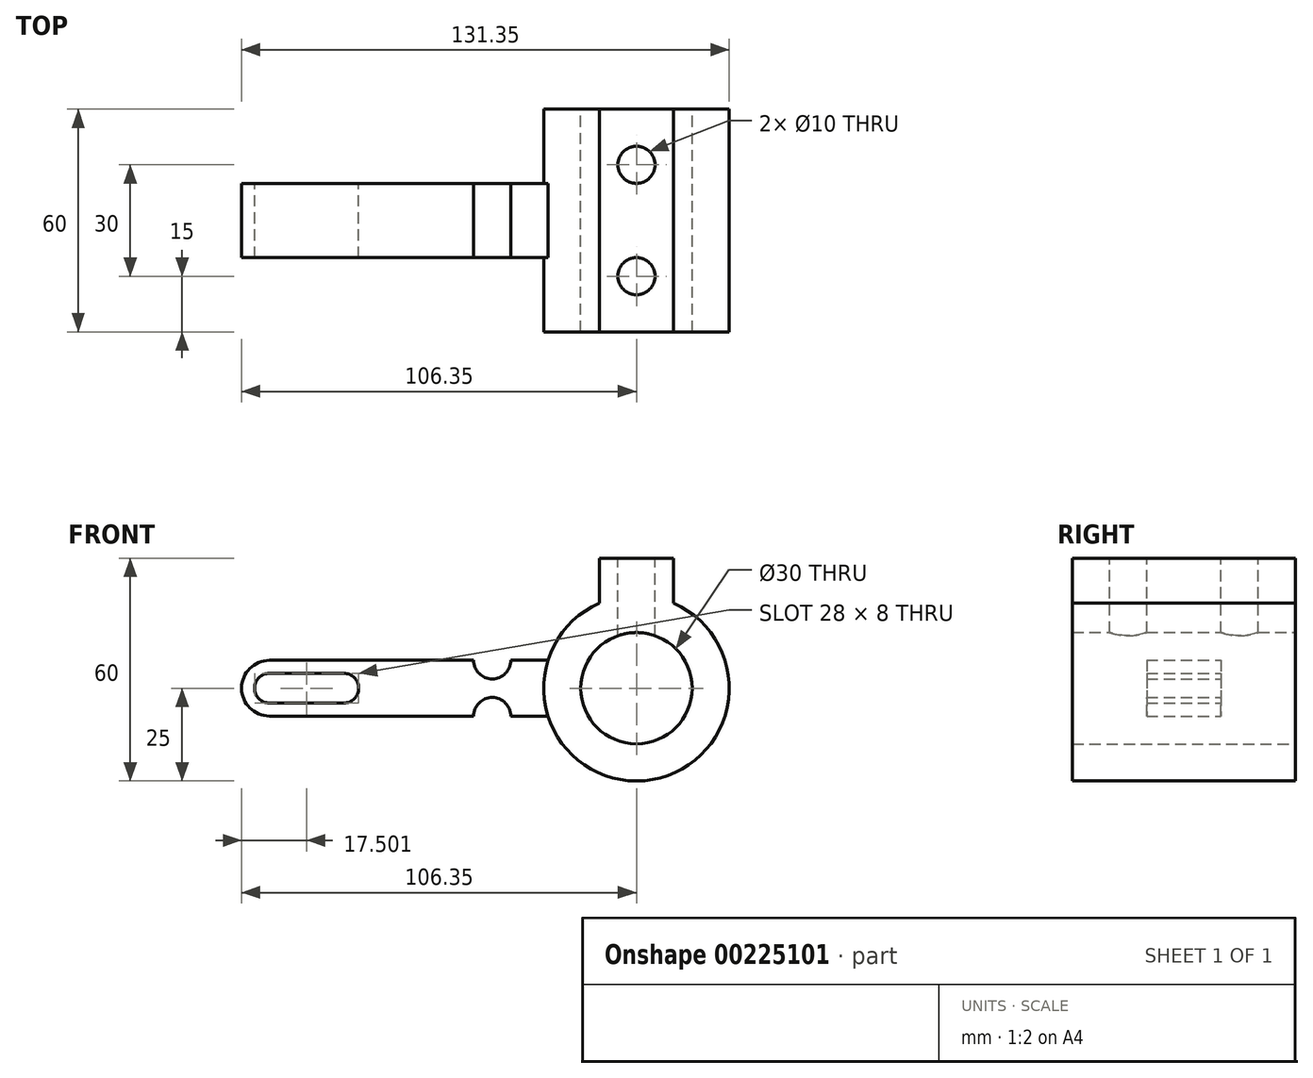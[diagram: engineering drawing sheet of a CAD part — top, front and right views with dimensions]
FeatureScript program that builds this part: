
annotation { "Feature Type Name" : "Feature", "Feature Type Description" : "" }
export const myFeature = defineFeature(function(context is Context, id is Id, definition is map)
    precondition{}
    {
        {
            var Q0;
            Q0=qCreatedBy(makeId("Front.planeOp"),FACE);
            var sketch = newSketch(context, id + "F0", { "sketchPlane" : qUnion([Q0])});
            skCircle(sketch, "E0", {"center": v(0, 0) * mm, "radius": 25 * mm});
            skCircle(sketch, "E1", {"center": v(0, 0) * mm, "radius": 15 * mm});
            skLineSegment(sketch, "E2.bottom", {"start": v(10, 15) * mm, "end": v(-10, 15) * mm});
            skLineSegment(sketch, "E2.top", {"start": v(10, 35) * mm, "end": v(-10, 35) * mm});
            skLineSegment(sketch, "E2.left", {"start": v(10, 15) * mm, "end": v(10, 35) * mm});
            skLineSegment(sketch, "E2.right", {"start": v(-10, 15) * mm, "end": v(-10, 35) * mm});
            skPoint(sketch, "E2.middle", {"position": v(0, 25) * mm});
            skLineSegment(sketch, "E3", {"start": v(-124.07, 0) * mm, "end": v(52.52, 0) * mm, "construction": true});
            skLineSegment(sketch, "E4", {"start": v(-124.07, 0) * mm, "end": v(-185.63, 0) * mm, "construction": true});
            skLineSegment(sketch, "E5.bottom", {"start": v(-23.85, 7.5) * mm, "end": v(-33.85, 7.5) * mm});
            skLineSegment(sketch, "E5.top", {"start": v(-23.85, -7.5) * mm, "end": v(-33.85, -7.5) * mm});
            skLineSegment(sketch, "E5.left", {"start": v(-23.85, 7.5) * mm, "end": v(-23.85, -7.5) * mm});
            skLineSegment(sketch, "E5.right", {"start": v(-98.85, 7.5) * mm, "end": v(-98.85, -7.5) * mm, "construction": true});
            skLineSegment(sketch, "E6", {"start": v(-38.85, 15.12) * mm, "end": v(-38.85, -23.72) * mm, "construction": true});
            skArc(sketch, "E7", {"start": v(-43.85, 7.5) * mm, "mid": v(-38.85, 2.5) * mm, "end": v(-33.85, 7.5) * mm});
            skArc(sketch, "E8", {"start": v(-33.85, -7.5) * mm, "mid": v(-38.85, -2.5) * mm, "end": v(-43.85, -7.5) * mm});
            skLineSegment(sketch, "E9.trimOffspring", {"start": v(-43.85, 7.5) * mm, "end": v(-98.85, 7.5) * mm});
            skLineSegment(sketch, "E10.trimOffspring", {"start": v(-43.85, -7.5) * mm, "end": v(-98.85, -7.5) * mm});
            skLineSegment(sketch, "E11", {"start": v(-78.85, 16.94) * mm, "end": v(-78.85, -16.42) * mm, "construction": true});
            skArc(sketch, "E12", {"start": v(-98.85, 7.5) * mm, "mid": v(-106.35, 0) * mm, "end": v(-98.85, -7.5) * mm});
            skArc(sketch, "E13", {"start": v(-98.85, 4) * mm, "mid": v(-102.85, 0) * mm, "end": v(-98.85, -4) * mm});
            skLineSegment(sketch, "E14", {"start": v(-98.85, 4) * mm, "end": v(-78.85, 4) * mm});
            skLineSegment(sketch, "E15", {"start": v(-98.85, -4) * mm, "end": v(-78.85, -4) * mm});
            skArc(sketch, "E16", {"start": v(-78.85, -4) * mm, "mid": v(-74.85, 0) * mm, "end": v(-78.85, 4) * mm});
            skPoint(sketch, "E16.centerSnap0", {"position": v(-78.85, 0.26) * mm});
            skSolve(sketch);
        }
        {
            var Q0;
            {var subQ3=sQuery(id+"F0.wireOp",EDGE,"E1");Q0=makeQuery(id+"F0.imprint","IMPRINT",FACE,{"disambiguationData":[TD([[makeQuery(id+"F0.imprint","IMPRINT",EDGE,{"derivedFrom":subQ3}),-1.0]])]});}
            var Q1;
            {var subQ3=sQuery(id+"F0.wireOp",EDGE,"E0");var subQ5=sQuery(id+"F0.wireOp",EDGE,"E2.right");var subQ8=makeQuery(id+"F0.imprint","INTERSECT",VERTEX,{"derivedFrom":[subQ3,subQ5]});Q1=makeQuery(id+"F0.imprint","IMPRINT",FACE,{"disambiguationData":[TD([[makeQuery(id+"F0.imprint","IMPRINT",EDGE,{"disambiguationData":[TD([[subQ8,1.0]])],"derivedFrom":subQ3}),1.0]])]});}
            var Q2;
            {var subQ0=sQuery(id+"F0.wireOp",EDGE,"E5.left");Q2=makeQuery(id+"F0.imprint","IMPRINT",FACE,{"disambiguationData":[TD([[makeQuery(id+"F0.imprint","IMPRINT",EDGE,{"derivedFrom":subQ0}),-1.0]])]});}
            var Q3;
            {var subQ5=sQuery(id+"F0.wireOp",EDGE,"E2.top");Q3=makeQuery(id+"F0.imprint","IMPRINT",FACE,{"disambiguationData":[TD([[makeQuery(id+"F0.imprint","IMPRINT",EDGE,{"derivedFrom":subQ5}),1.0]])]});}
            extrude(context, id + "F1", {"entities" : qUnion([Q0, Q1, Q2, Q3]), "endBound" : BoundingType.SYMMETRIC, "depth" : 60 * mm});
        }
        {
            var Q0;
            {var subQ1=sQuery(id+"F0.wireOp",EDGE,"E5.bottom");Q0=makeQuery(id+"F0.imprint","IMPRINT",FACE,{"disambiguationData":[TD([[makeQuery(id+"F0.imprint","IMPRINT",EDGE,{"derivedFrom":subQ1}),1.0]])]});}
            extrude(context, id + "F2", {"entities" : qUnion([Q0]), "operationType" : NewBodyOperationType.ADD, "endBound" : BoundingType.SYMMETRIC, "depth" : 20 * mm});
        }
        {
            var Q0;
            Q0=makeQuery(id+"F1.opExtrude","SWEPT_FACE",FACE,{"disambiguationData":[OSD([sQuery(id+"F0.wireOp",EDGE,"E2.top")])]});
            var sketch = newSketch(context, id + "F3", { "sketchPlane" : qUnion([Q0])});
            skCircle(sketch, "E17", {"center": v(0, 15) * mm, "radius": 5 * mm});
            skCircle(sketch, "E18", {"center": v(0, -15) * mm, "radius": 5 * mm});
            skSolve(sketch);
        }
        {
            var Q0;
            Q0=makeQuery(id+"F3.imprint","IMPRINT",FACE,{"disambiguationData":[TD([[makeQuery(id+"F3.imprint","IMPRINT",EDGE,{"derivedFrom":sQuery(id+"F3.wireOp",EDGE,"E17")}),1.0]])]});
            var Q1;
            Q1=makeQuery(id+"F3.imprint","IMPRINT",FACE,{"disambiguationData":[TD([[makeQuery(id+"F3.imprint","IMPRINT",EDGE,{"derivedFrom":sQuery(id+"F3.wireOp",EDGE,"E18")}),1.0]])]});
            extrude(context, id + "F4", {"entities" : qUnion([Q0, Q1]), "operationType" : NewBodyOperationType.REMOVE, "endBound" : BoundingType.UP_TO_NEXT, "oppositeDirection" : true, "depth" : 25 * mm});
        }
    });
